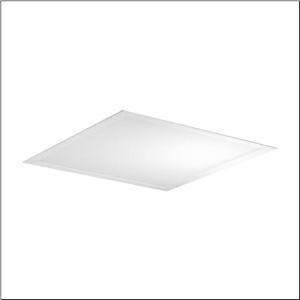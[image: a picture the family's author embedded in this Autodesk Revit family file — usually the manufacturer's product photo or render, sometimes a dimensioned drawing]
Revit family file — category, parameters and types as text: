
# Revit family: apollon_r__21_square_51mq11wd2414m_9dde
name_source: partatom
category: Lighting Fixtures
units: mm (PartAtom-declared; Revit-internal decimal feet)

## family parameters
Cut with Voids When Loaded = No
Host = Face
Light Source = No
Part Type = Normal
Room Calculation Point = No
Round Connector Dimension = Use Diameter
Shared = No

## types (1)
- Apollon® 21 square (1 x LED, 4200 lm, 24.7 W, 4000K)
    Apparent Load = 25 VA
    CIE Flux Codes = 60 87 97 100 100
    Color Rendering = 80
    Color Temperature = 4000K
    Default Elevation = 1800 mm
    Description = Apollon® 21 square, office luminaire, primary optical cover: micro prismatic cover, of PMMA, CAT 2 (L<= 3000cd/m²), light emission: direct distribution, primary light characteristic: symmetric, installation type: lay-in mounting, LED, rated luminous flux: 4.200lm, luminous efficacy: 170lm/W, light colour: 840, colour temperature: 4000K, with terminal, 5-pole, mains connection: 220..240V, AC/DC, 0/50..60Hz, rated input power: 24.7W, housing, of aluminium, coated, traffic white (RAL 9016), module: M625, length: 620mm, width: 620mm, height: 30mm, housing upper side, of sheet steel, galvanised, protection rating (complete): IP20, protection rating (lamp compartment, on room side): IP50, insulation class (complete): insulation class II (safety insulation), certification: CE, ENEC, impact resistance: IK03, permissible operating ambient temperature: -20..+45°C, permissible storage temperature: -40..+80°C, packaging unit: set of 5
    Height = 0 mm  [stored 0 ft]
    Lamp = 1 x LED
    Lamp Light Flux = 4200 lm
    Lamp Power = 24.7 W
    Lamp count = 1
    Length = 620 mm
    Luminous efficacy = 170 lm/W
    Manufacturer = Siteco
    ModVariant = No
    Model = 51MQ11WD2414M
    Mounting Place = Ceiling
    Mounting Type = Recessed
    Number of Poles = 1
    OnlyDefault = Yes
    Power Factor = 1
    Product Name = Apollon® 21 square
    Product group = office luminaire | ceiling recessed
    ProductGroupID = 401
    Protection Class = Protection class II
    Protection Degree = IP 20
    RLX_Detail_Level = 1
    RLX_Emergency_Light_Flux = 0 lm
    RLX_Emergency_Type = 0
    RLX_Emergency_Type_DB = No
    RlxData = <blob elided: 12965 chars, md5=8b420e17>
    Socket = socket
    Standby Power = 0 W
    System Light Flux = 4200 lm
    System Power = 25 W
    Type Comments = Product without accessories
    Type Image = l_1291054.jpg
    URL = http://relux.com
    VarID = ---
    Voltage = 0 V
    Weight = 0.00 kg
    Width = 620 mm

note: [stored X ft] marks values corroborated as IEEE doubles in the binary element streams (Revit-internal decimal feet)

## geometry (parser evidence)
native form markers: Sweep x8
no freeform markers — native parametric forms only
